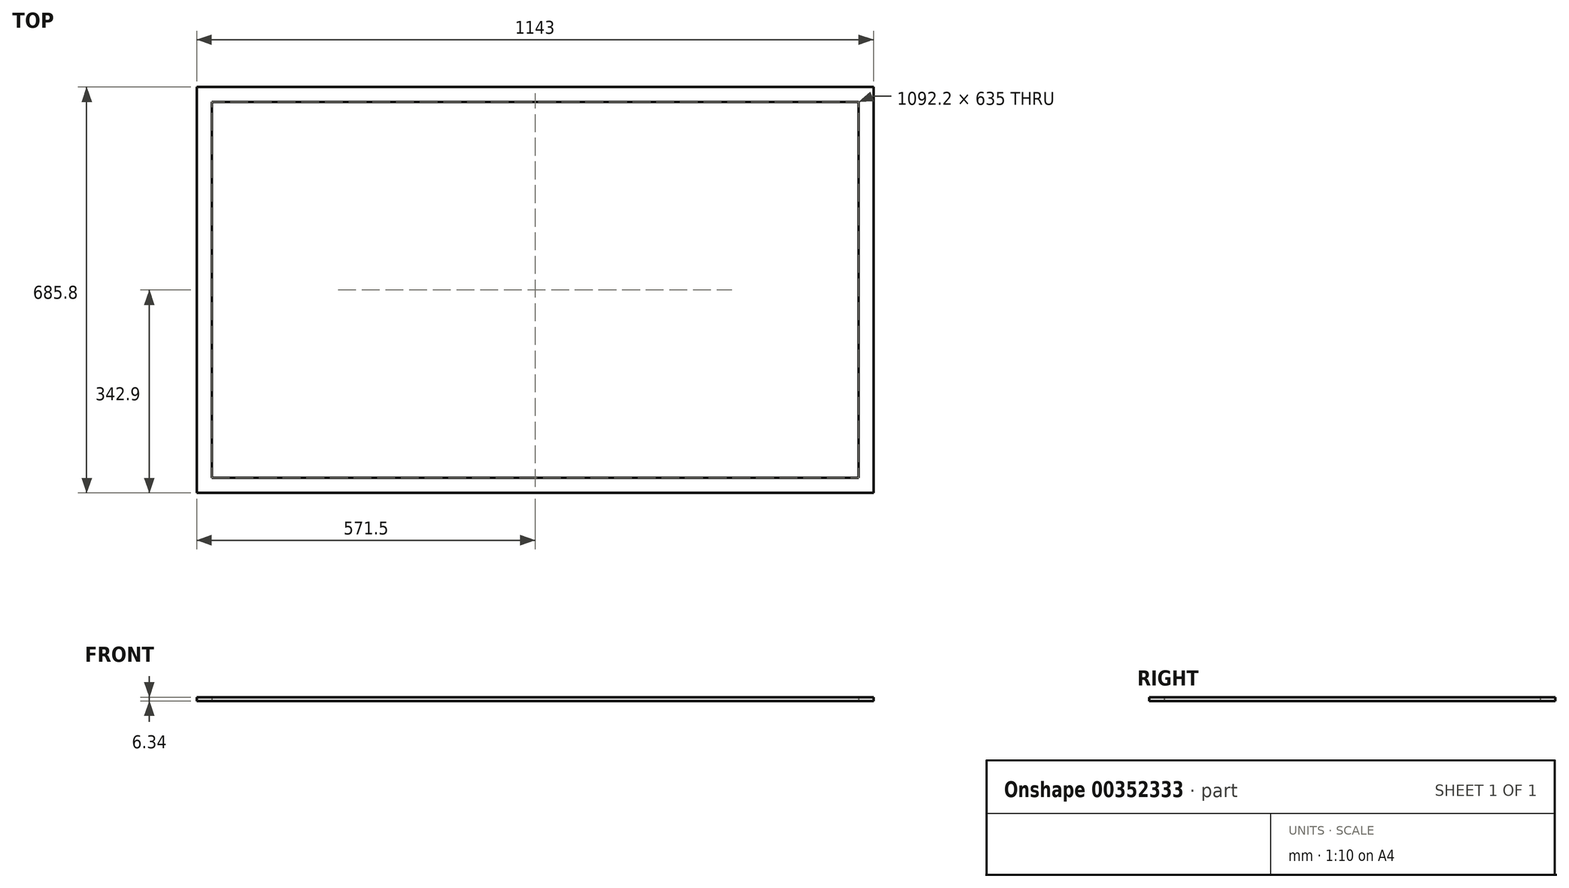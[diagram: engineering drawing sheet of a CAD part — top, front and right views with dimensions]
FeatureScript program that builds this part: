
annotation { "Feature Type Name" : "Feature", "Feature Type Description" : "" }
export const myFeature = defineFeature(function(context is Context, id is Id, definition is map)
    precondition{}
    {
        {
            var Q0;
            Q0=qCreatedBy(makeId("Top.planeOp"),FACE);
            var sketch = newSketch(context, id + "F0", { "sketchPlane" : qUnion([Q0])});
            skPoint(sketch, "E0.middle", {"position": v(0, 0) * mm});
            skLineSegment(sketch, "E1.bottom", {"start": v(546.1, 317.5) * mm, "end": v(-546.1, 317.5) * mm});
            skLineSegment(sketch, "E1.top", {"start": v(546.1, -317.5) * mm, "end": v(-546.1, -317.5) * mm});
            skLineSegment(sketch, "E1.left", {"start": v(546.1, 317.5) * mm, "end": v(546.1, -317.5) * mm});
            skLineSegment(sketch, "E1.right", {"start": v(-546.1, 317.5) * mm, "end": v(-546.1, -317.5) * mm});
            skLineSegment(sketch, "E2.bottom", {"start": v(-571.5, -342.9) * mm, "end": v(571.5, -342.9) * mm});
            skLineSegment(sketch, "E2.top", {"start": v(-571.5, 342.9) * mm, "end": v(571.5, 342.9) * mm});
            skLineSegment(sketch, "E2.left", {"start": v(-571.5, -342.9) * mm, "end": v(-571.5, 342.9) * mm});
            skLineSegment(sketch, "E2.right", {"start": v(571.5, -342.9) * mm, "end": v(571.5, 342.9) * mm});
            skSolve(sketch);
        }
        {
            var Q0;
            Q0=makeQuery(id+"F0.imprint","IMPRINT",FACE,{"disambiguationData":[TD([[makeQuery(id+"F0.imprint","IMPRINT",EDGE,{"derivedFrom":sQuery(id+"F0.wireOp",EDGE,"E1.bottom")}),-1.0]])]});
            extrude(context, id + "F1", {"entities" : qUnion([Q0]), "endBound" : BoundingType.SYMMETRIC, "depth" : 6.35 * mm});
        }
    });
